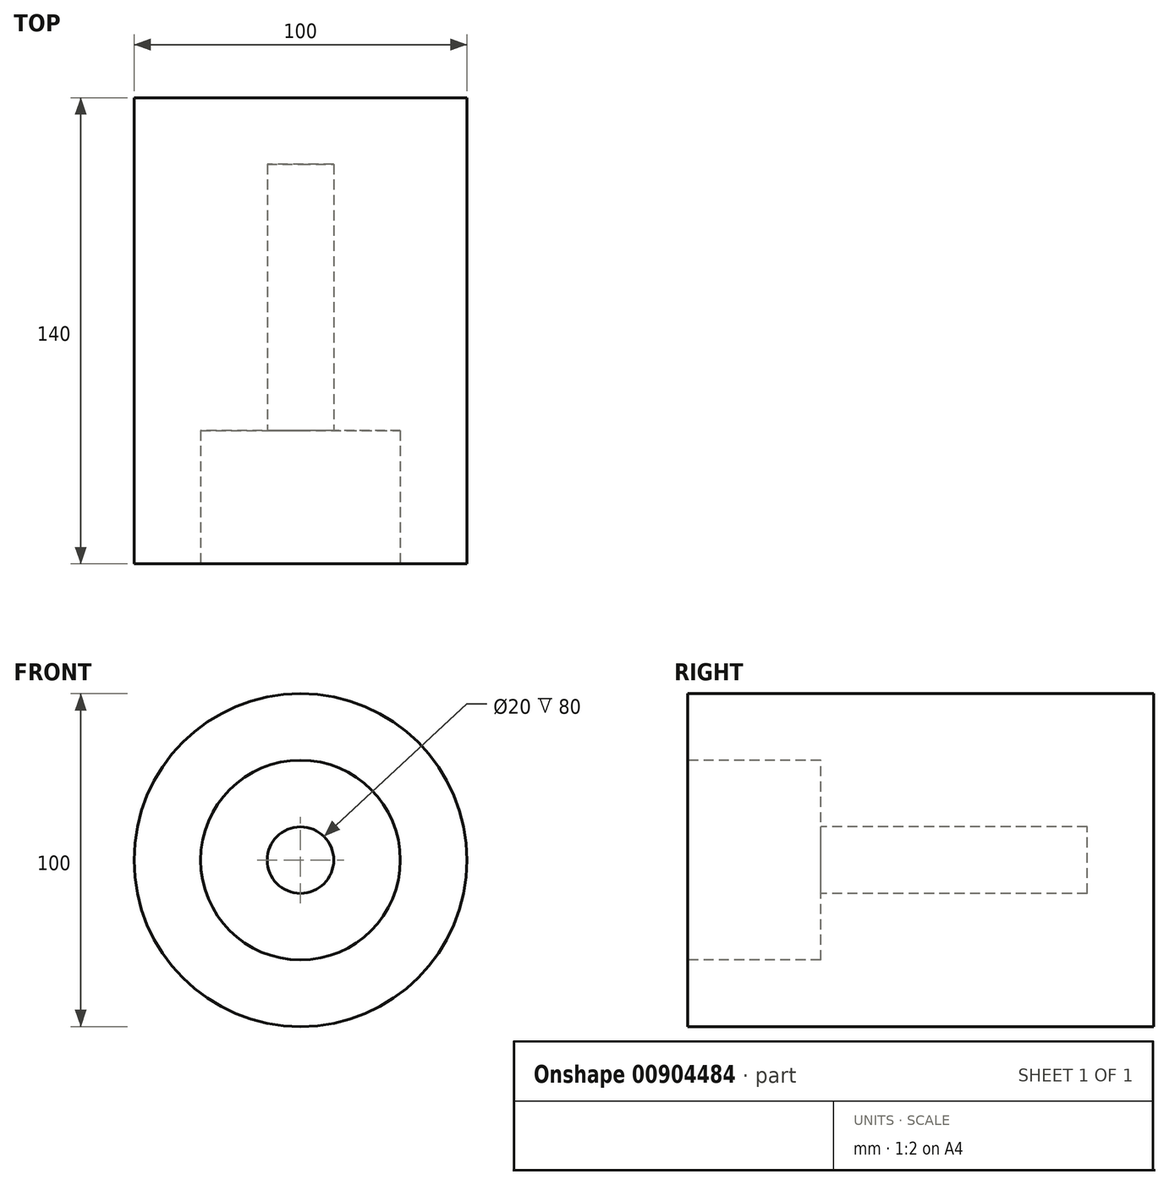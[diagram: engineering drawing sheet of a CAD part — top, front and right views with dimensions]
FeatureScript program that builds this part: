
annotation { "Feature Type Name" : "Feature", "Feature Type Description" : "" }
export const myFeature = defineFeature(function(context is Context, id is Id, definition is map)
    precondition{}
    {
        {
            var Q0;
            Q0=qCreatedBy(makeId("Front.planeOp"),FACE);
            var sketch = newSketch(context, id + "F0", { "sketchPlane" : qUnion([Q0])});
            skCircle(sketch, "E0", {"center": v(0, 0) * mm, "radius": 50 * mm});
            skCircle(sketch, "E1", {"center": v(0, 0) * mm, "radius": 30 * mm});
            skCircle(sketch, "E2", {"center": v(0, 0) * mm, "radius": 10 * mm});
            skSolve(sketch);
        }
        {
            var Q0;
            Q0=makeQuery(id+"F0.imprint","IMPRINT",FACE,{"disambiguationData":[TD([[makeQuery(id+"F0.imprint","IMPRINT",EDGE,{"derivedFrom":sQuery(id+"F0.wireOp",EDGE,"E0")}),1.0]])]});
            var Q1;
            Q1=makeQuery(id+"F0.imprint","IMPRINT",FACE,{"disambiguationData":[TD([[makeQuery(id+"F0.imprint","IMPRINT",EDGE,{"derivedFrom":sQuery(id+"F0.wireOp",EDGE,"E1")}),1.0]])]});
            var Q2;
            Q2=makeQuery(id+"F0.imprint","IMPRINT",FACE,{"disambiguationData":[TD([[makeQuery(id+"F0.imprint","IMPRINT",EDGE,{"derivedFrom":sQuery(id+"F0.wireOp",EDGE,"E2")}),1.0]])]});
            extrude(context, id + "F1", {"entities" : qUnion([Q0, Q1, Q2]), "depth" : 70 * mm, "offsetDistance" : 25.4 * mm});
        }
        {
            var Q0;
            Q0=makeQuery(id+"F1.opExtrude","CAP_FACE",FACE,{"disambiguationData":[OSD([sQuery(id+"F0.wireOp",EDGE,"E0")])],"isStart":true});
            var Q1;
            Q1=makeQuery(id+"F1.opExtrude","CAP_FACE",FACE,{"disambiguationData":[OSD([sQuery(id+"F0.wireOp",EDGE,"E0")])],"isStart":false});
            extrude(context, id + "F2", {"entities" : qUnion([Q0, Q1]), "operationType" : NewBodyOperationType.ADD, "depth" : 70 * mm, "offsetDistance" : 25.4 * mm});
        }
        {
            var Q0;
            Q0=makeQuery(id+"F1.opExtrude","CAP_FACE",FACE,{"disambiguationData":[OSD([sQuery(id+"F0.wireOp",EDGE,"E0")])],"isStart":false});
            var sketch = newSketch(context, id + "F3", { "sketchPlane" : qUnion([Q0])});
            skCircle(sketch, "E3", {"center": v(0, 0) * mm, "radius": 10 * mm});
            skSolve(sketch);
        }
        {
            var Q0;
            Q0=makeQuery(id+"F3.imprint","IMPRINT",FACE,{"disambiguationData":[TD([[makeQuery(id+"F3.imprint","IMPRINT",EDGE,{"derivedFrom":sQuery(id+"F3.wireOp",EDGE,"E3")}),1.0]])]});
            extrude(context, id + "F4", {"entities" : qUnion([Q0]), "operationType" : NewBodyOperationType.REMOVE, "oppositeDirection" : true, "depth" : 120 * mm, "offsetDistance" : 25.4 * mm});
        }
        {
            var Q0;
            Q0=makeQuery(id+"F1.opExtrude","CAP_FACE",FACE,{"disambiguationData":[OSD([sQuery(id+"F0.wireOp",EDGE,"E0")])],"isStart":false});
            var sketch = newSketch(context, id + "F5", { "sketchPlane" : qUnion([Q0])});
            skCircle(sketch, "E4", {"center": v(0, 0) * mm, "radius": 30 * mm});
            skSolve(sketch);
        }
        {
            var Q0;
            Q0=makeQuery(id+"F5.imprint","IMPRINT",FACE,{"disambiguationData":[TD([[makeQuery(id+"F5.imprint","IMPRINT",EDGE,{"derivedFrom":sQuery(id+"F5.wireOp",EDGE,"E4")}),1.0]])]});
            extrude(context, id + "F6", {"entities" : qUnion([Q0]), "operationType" : NewBodyOperationType.REMOVE, "oppositeDirection" : true, "depth" : 40 * mm, "offsetDistance" : 25.4 * mm});
        }
    });
